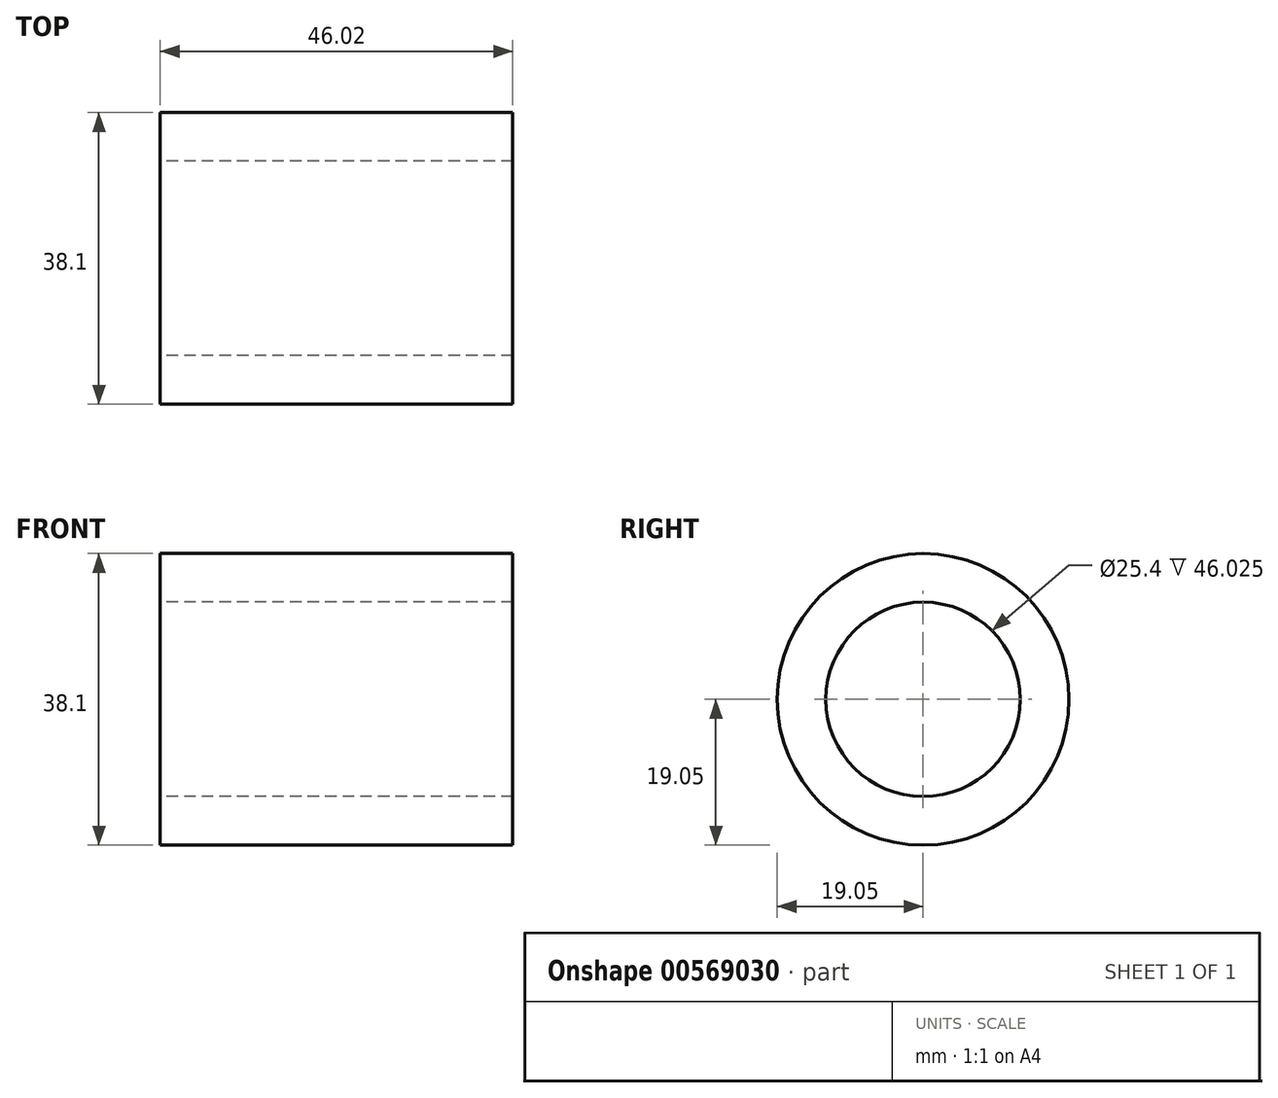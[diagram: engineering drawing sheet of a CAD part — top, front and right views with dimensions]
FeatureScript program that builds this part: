
annotation { "Feature Type Name" : "Feature", "Feature Type Description" : "" }
export const myFeature = defineFeature(function(context is Context, id is Id, definition is map)
    precondition{}
    {
        {
            var Q0;
            Q0=qCreatedBy(makeId("Right.planeOp"),FACE);
            var sketch = newSketch(context, id + "F0", { "sketchPlane" : qUnion([Q0])});
            skCircle(sketch, "E0", {"center": v(0, 0) * mm, "radius": 19.05 * mm});
            skSolve(sketch);
        }
        {
            var Q0;
            Q0=makeQuery(id+"F0.imprint","IMPRINT",FACE,{"disambiguationData":[TD([[makeQuery(id+"F0.imprint","IMPRINT",EDGE,{"derivedFrom":sQuery(id+"F0.wireOp",EDGE,"E0")}),1.0]])]});
            extrude(context, id + "F1", {"entities" : qUnion([Q0]), "depth" : 46.02 * mm, "offsetDistance" : 25.4 * mm});
        }
        {
            var Q0;
            Q0=sQuery(id+"F0.wireOp",VERTEX,"E0.center");
            var Q1;
            Q1=makeQuery(id+"F1.opExtrude","SWEPT_BODY",BODY,{"disambiguationData":[OSD([sQuery(id+"F0.wireOp",EDGE,"E0")])]});
            hole(context, id + "F2", {"style" : HoleStyle.SIMPLE, "endStyle" : HoleEndStyle.BLIND, "oppositeDirection" : true, "holeDiameter" : 25.4 * mm, "holeDepth" : 46.02 * mm, "isTappedThrough" : true, "tappedDepth" : 12.7 * mm, "tapClearance" : 3, "startFromSketch" : true, "locations" : qUnion([Q0]), "scope" : qUnion([Q1]), "majorDiameter" : 6.35 * mm});
        }
    });
